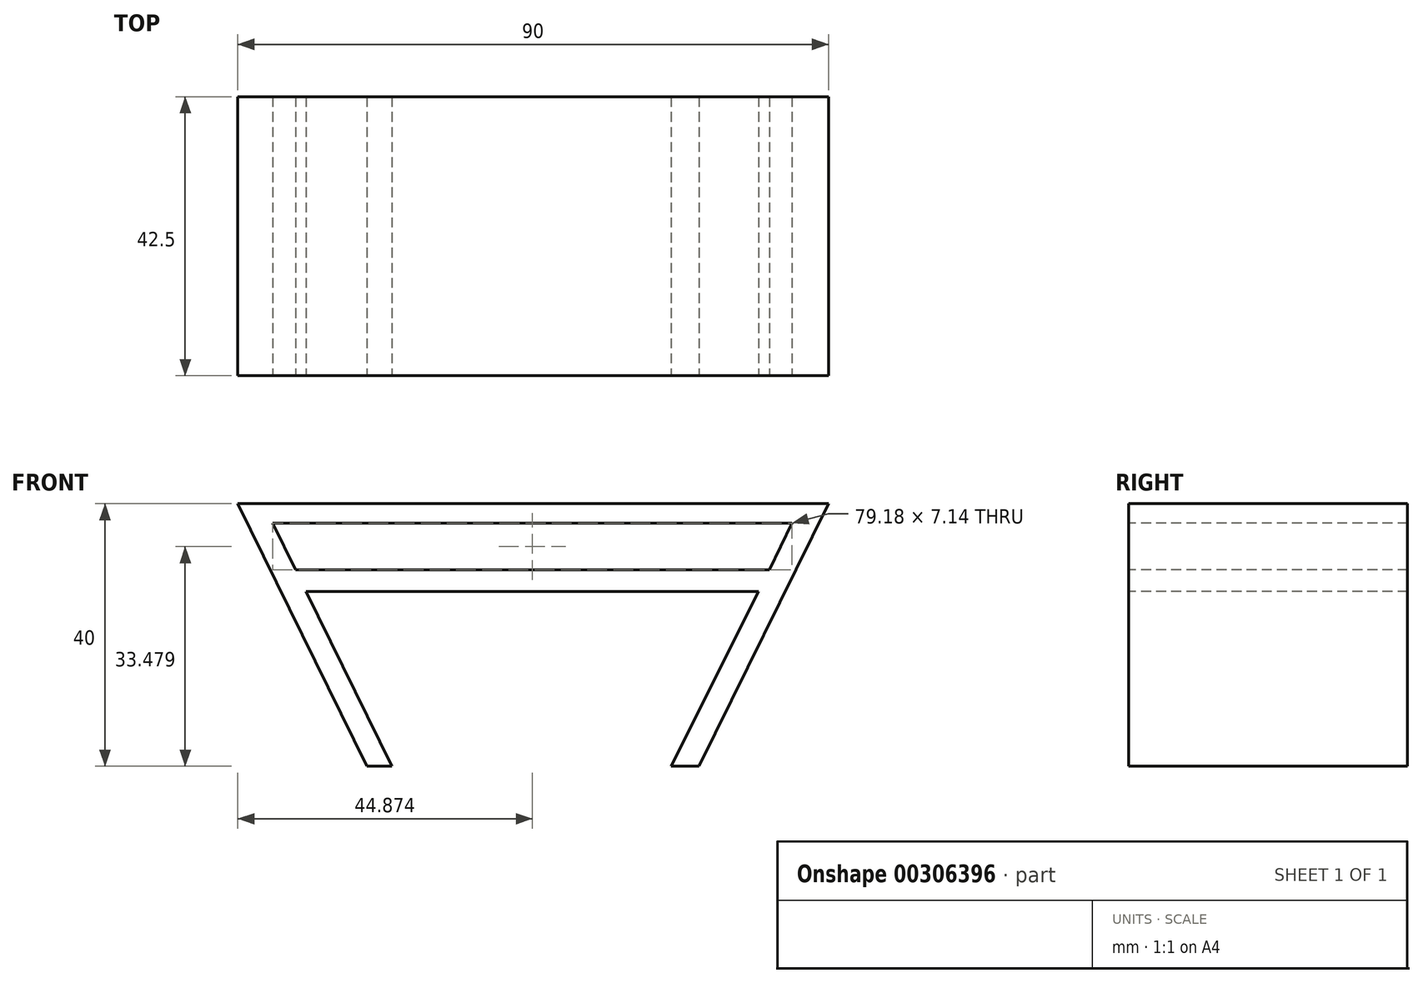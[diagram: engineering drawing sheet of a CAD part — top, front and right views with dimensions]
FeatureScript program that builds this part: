
annotation { "Feature Type Name" : "Feature", "Feature Type Description" : "" }
export const myFeature = defineFeature(function(context is Context, id is Id, definition is map)
    precondition{}
    {
        {
            var Q0;
            Q0=qCreatedBy(makeId("Front.planeOp"),FACE);
            var sketch = newSketch(context, id + "F0", { "sketchPlane" : qUnion([Q0])});
            skLineSegment(sketch, "E0.bottom", {"start": v(-85.28, 51.99) * mm, "end": v(94.72, 51.99) * mm});
            skLineSegment(sketch, "E0.top", {"start": v(-85.28, -28.01) * mm, "end": v(94.72, -28.01) * mm});
            skLineSegment(sketch, "E0.left", {"start": v(-85.28, 51.99) * mm, "end": v(-85.28, -28.01) * mm});
            skLineSegment(sketch, "E0.right", {"start": v(94.72, 51.99) * mm, "end": v(94.72, -28.01) * mm});
            skSolve(sketch);
        }
        {
            var Q0;
            Q0=makeQuery(id+"F0.imprint","IMPRINT",FACE,{"disambiguationData":[TD([[makeQuery(id+"F0.imprint","IMPRINT",EDGE,{"derivedFrom":sQuery(id+"F0.wireOp",EDGE,"E0.bottom")}),-1.0]])]});
            extrude(context, id + "F1", {"entities" : qUnion([Q0]), "depth" : 85 * mm});
        }
        {
            var Q0;
            Q0=makeQuery(id+"F1.opExtrude","CAP_FACE",FACE,{"disambiguationData":[OSD([sQuery(id+"F0.wireOp",EDGE,"E0.bottom"),sQuery(id+"F0.wireOp",EDGE,"E0.top"),sQuery(id+"F0.wireOp",EDGE,"E0.left"),sQuery(id+"F0.wireOp",EDGE,"E0.right")])],"isStart":false});
            var sketch = newSketch(context, id + "F2", { "sketchPlane" : qUnion([Q0])});
            skLineSegment(sketch, "E1", {"start": v(-85.28, 51.99) * mm, "end": v(-46, -28.01) * mm});
            skLineSegment(sketch, "E2", {"start": v(94.72, 51.99) * mm, "end": v(55.23, -28.01) * mm});
            skSolve(sketch);
        }
        {
            var Q0;
            Q0=qSketchRegion(id+"F2",true);
            var Q1;
            {var subQ0=sQuery(id+"F2.wireOp",EDGE,"E1");Q1=makeQuery(id+"F2.imprint","IMPRINT",FACE,{"disambiguationData":[TD([[makeQuery(id+"F2.imprint","IMPRINT",EDGE,{"derivedFrom":subQ0}),-1.0]])]});}
            var Q2;
            {var subQ0=sQuery(id+"F2.wireOp",EDGE,"E2");Q2=makeQuery(id+"F2.imprint","IMPRINT",FACE,{"disambiguationData":[TD([[makeQuery(id+"F2.imprint","IMPRINT",EDGE,{"derivedFrom":subQ0}),1.0]])]});}
            extrude(context, id + "F3", {"entities" : qUnion([Q0, Q1, Q2]), "operationType" : NewBodyOperationType.REMOVE, "endBound" : BoundingType.THROUGH_ALL, "oppositeDirection" : true, "depth" : 25 * mm});
        }
        {
            var Q0;
            Q0=makeQuery(id+"F1.opExtrude","CAP_FACE",FACE,{"disambiguationData":[OSD([sQuery(id+"F0.wireOp",EDGE,"E0.bottom"),sQuery(id+"F0.wireOp",EDGE,"E0.top"),sQuery(id+"F0.wireOp",EDGE,"E0.left"),sQuery(id+"F0.wireOp",EDGE,"E0.right")])],"isStart":false});
            var sketch = newSketch(context, id + "F4", { "sketchPlane" : qUnion([Q0])});
            skLineSegment(sketch, "E3", {"start": v(-75.37, 31.8) * mm, "end": v(84.76, 31.8) * mm});
            skLineSegment(sketch, "E4", {"start": v(-72.17, 25.3) * mm, "end": v(81.54, 25.3) * mm});
            skLineSegment(sketch, "E5", {"start": v(-77.61, 51.99) * mm, "end": v(-67.7, 31.8) * mm});
            skLineSegment(sketch, "E6", {"start": v(-67.7, 31.8) * mm, "end": v(-38.34, -28.01) * mm});
            skLineSegment(sketch, "E7", {"start": v(86.53, 51.99) * mm, "end": v(76.7, 31.8) * mm});
            skLineSegment(sketch, "E8", {"start": v(76.7, 31.8) * mm, "end": v(46.69, -28.01) * mm});
            skLineSegment(sketch, "E9", {"start": v(-74.7, 46.07) * mm, "end": v(83.65, 46.07) * mm});
            skSolve(sketch);
        }
        {
            var Q0;
            {var subQ5=sQuery(id+"F4.wireOp",EDGE,"E9");Q0=makeQuery(id+"F4.imprint","IMPRINT",FACE,{"disambiguationData":[TD([[makeQuery(id+"F4.imprint","IMPRINT",EDGE,{"derivedFrom":subQ5}),-1.0]])]});}
            var Q1;
            {var subQ0=sQuery(id+"F4.wireOp",EDGE,"E6");var subQ1=sQuery(id+"F4.wireOp",EDGE,"E4");var subQ2=makeQuery(id+"F4.imprint","INTERSECT",VERTEX,{"derivedFrom":[subQ1,subQ0]});Q1=makeQuery(id+"F4.imprint","IMPRINT",FACE,{"disambiguationData":[TD([[makeQuery(id+"F4.imprint","IMPRINT",EDGE,{"disambiguationData":[TD([[subQ2,-1.0]])],"derivedFrom":subQ1}),-1.0]])]});}
            extrude(context, id + "F5", {"entities" : qUnion([Q0, Q1]), "operationType" : NewBodyOperationType.REMOVE, "endBound" : BoundingType.THROUGH_ALL, "oppositeDirection" : true, "depth" : 25 * mm});
        }
        {
            var Q0;
            Q0=makeQuery(id+"F1.opExtrude","SWEPT_BODY",BODY,{"disambiguationData":[OSD([sQuery(id+"F0.wireOp",EDGE,"E0.bottom"),sQuery(id+"F0.wireOp",EDGE,"E0.top"),sQuery(id+"F0.wireOp",EDGE,"E0.left"),sQuery(id+"F0.wireOp",EDGE,"E0.right")])]});
            var Q1;
            Q1=qCreatedBy(makeId("Origin.pointOp"),VERTEX);
            transform(context, id + "F6", {"entities" : qUnion([Q0]), "transformType" : TransformType.SCALE_UNIFORMLY, "scale" : 0.5, "scalePoint" : qUnion([Q1]), "makeCopy" : false});
        }
    });
